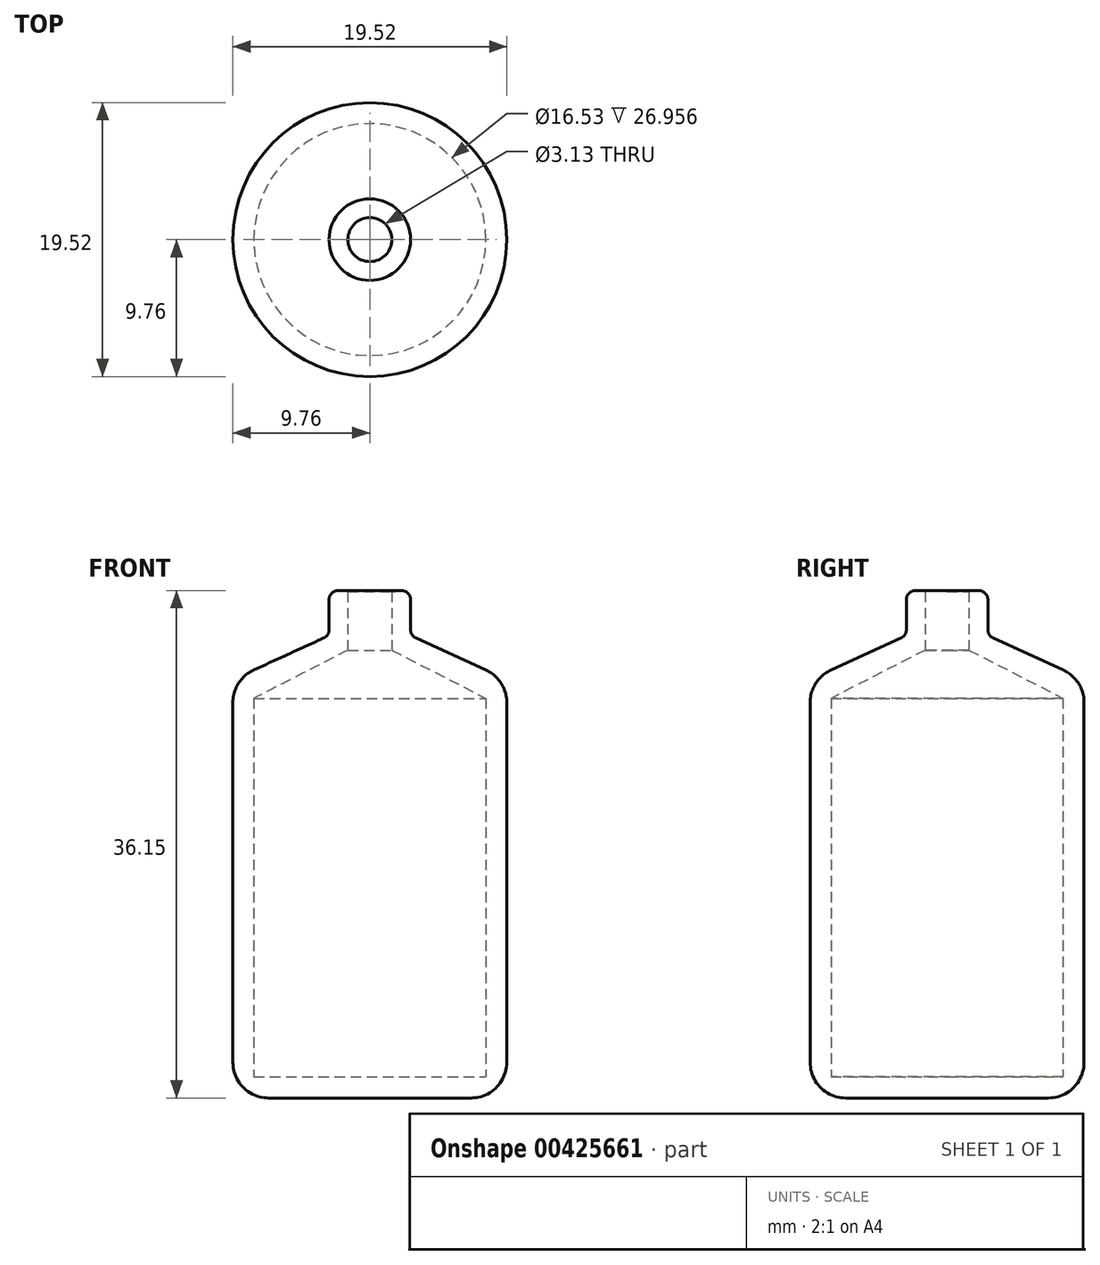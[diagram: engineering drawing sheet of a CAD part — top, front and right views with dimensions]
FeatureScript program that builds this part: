
annotation { "Feature Type Name" : "Feature", "Feature Type Description" : "" }
export const myFeature = defineFeature(function(context is Context, id is Id, definition is map)
    precondition{}
    {
        {
            var Q0;
            Q0=qCreatedBy(makeId("Front.planeOp"),FACE);
            var sketch = newSketch(context, id + "F0", { "sketchPlane" : qUnion([Q0])});
            skLineSegment(sketch, "E0", {"start": v(0, 0) * mm, "end": v(-9.76, 0) * mm});
            skLineSegment(sketch, "E1", {"start": v(-9.76, 0) * mm, "end": v(-9.76, 29.82) * mm});
            skLineSegment(sketch, "E2", {"start": v(-9.76, 29.82) * mm, "end": v(-2.9, 32.95) * mm});
            skLineSegment(sketch, "E3", {"start": v(-2.9, 32.95) * mm, "end": v(-2.9, 36.22) * mm});
            skLineSegment(sketch, "E4", {"start": v(0, 0) * mm, "end": v(0, 1.52) * mm});
            skLineSegment(sketch, "E5", {"start": v(0, 1.52) * mm, "end": v(-8.27, 1.52) * mm});
            skLineSegment(sketch, "E6", {"start": v(-8.27, 1.52) * mm, "end": v(-8.27, 28.48) * mm});
            skLineSegment(sketch, "E7", {"start": v(-8.27, 28.48) * mm, "end": v(-1.56, 31.9) * mm});
            skLineSegment(sketch, "E8", {"start": v(-1.56, 31.9) * mm, "end": v(-1.56, 36.08) * mm});
            skLineSegment(sketch, "E9", {"start": v(-1.56, 36.08) * mm, "end": v(-2.9, 36.22) * mm});
            skSolve(sketch);
        }
        {
            var Q0;
            Q0 = qSketchRegion(id + "F0", true);
            var Q1;
            Q1=sQuery(id+"F0.wireOp",EDGE,"E4");
            revolve(context, id + "F1", {"entities" : qUnion([Q0]), "axis" : qUnion([Q1]), "revolveType" : RevolveType.FULL});
        }
        {
            var Q0;
            Q0=makeQuery(id+"F1.opRevolve","SWEPT_FACE",FACE,{"disambiguationData":[OSD([sQuery(id+"F0.wireOp",EDGE,"E1")])]});
            fillet(context, id + "F2", {"entities" : qUnion([Q0]), "radius" : 2.54 * mm, "tangentPropagation" : true, "allowEdgeOverflow" : false});
        }
        {
            var Q0;
            Q0=makeQuery(id+"F1.opRevolve","SWEPT_EDGE",EDGE,{"disambiguationData":[OSD([sQuery(id+"F0.wireOp",EDGE,"E3"),sQuery(id+"F0.wireOp",EDGE,"E9")])]});
            fillet(context, id + "F3", {"entities" : qUnion([Q0]), "radius" : 0.64 * mm, "tangentPropagation" : true, "allowEdgeOverflow" : false});
        }
        {
            var Q0;
            Q0=makeQuery(id+"F1.opRevolve","SWEPT_EDGE",EDGE,{"disambiguationData":[OSD([sQuery(id+"F0.wireOp",EDGE,"E2"),sQuery(id+"F0.wireOp",EDGE,"E3")])]});
            fillet(context, id + "F4", {"entities" : qUnion([Q0]), "radius" : 0.64 * mm, "tangentPropagation" : true, "allowEdgeOverflow" : false});
        }
    });
